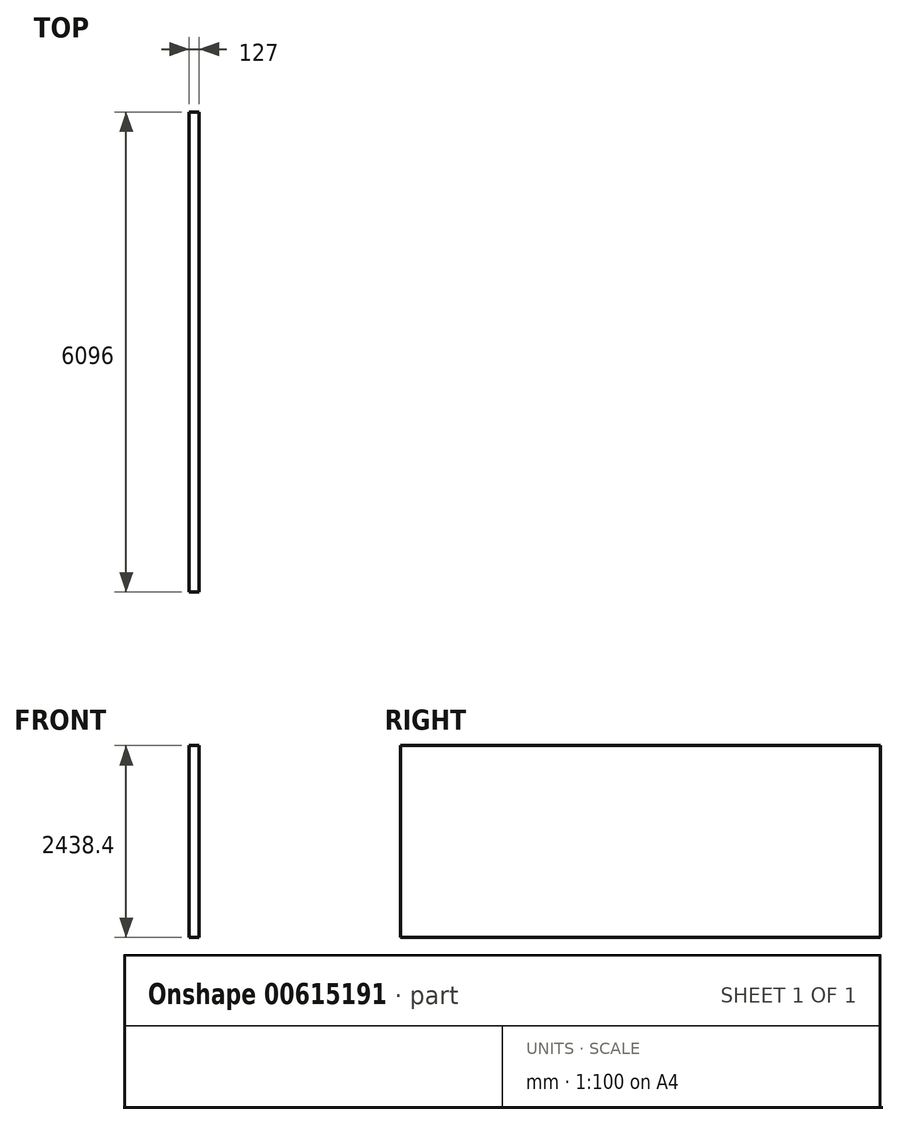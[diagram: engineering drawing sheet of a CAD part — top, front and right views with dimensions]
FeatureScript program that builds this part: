
annotation { "Feature Type Name" : "Feature", "Feature Type Description" : "" }
export const myFeature = defineFeature(function(context is Context, id is Id, definition is map)
    precondition{}
    {
        {
            var Q0;
            Q0=qCreatedBy(makeId("Right.planeOp"),FACE);
            var sketch = newSketch(context, id + "F0", { "sketchPlane" : qUnion([Q0])});
            skLineSegment(sketch, "E0.bottom", {"start": v(-69.94, -64.61) * mm, "end": v(6026.06, -64.61) * mm});
            skLineSegment(sketch, "E0.top", {"start": v(-69.94, 2373.79) * mm, "end": v(6026.06, 2373.79) * mm});
            skLineSegment(sketch, "E0.left", {"start": v(-69.94, -64.61) * mm, "end": v(-69.94, 2373.79) * mm});
            skLineSegment(sketch, "E0.right", {"start": v(6026.06, -64.61) * mm, "end": v(6026.06, 2373.79) * mm});
            skSolve(sketch);
        }
        {
            var Q0;
            Q0=makeQuery(id+"F0.imprint","IMPRINT",FACE,{"disambiguationData":[TD([[makeQuery(id+"F0.imprint","IMPRINT",EDGE,{"derivedFrom":sQuery(id+"F0.wireOp",EDGE,"E0.bottom")}),1.0]])]});
            extrude(context, id + "F1", {"entities" : qUnion([Q0]), "depth" : 127 * mm, "offsetDistance" : 25.4 * mm});
        }
    });
